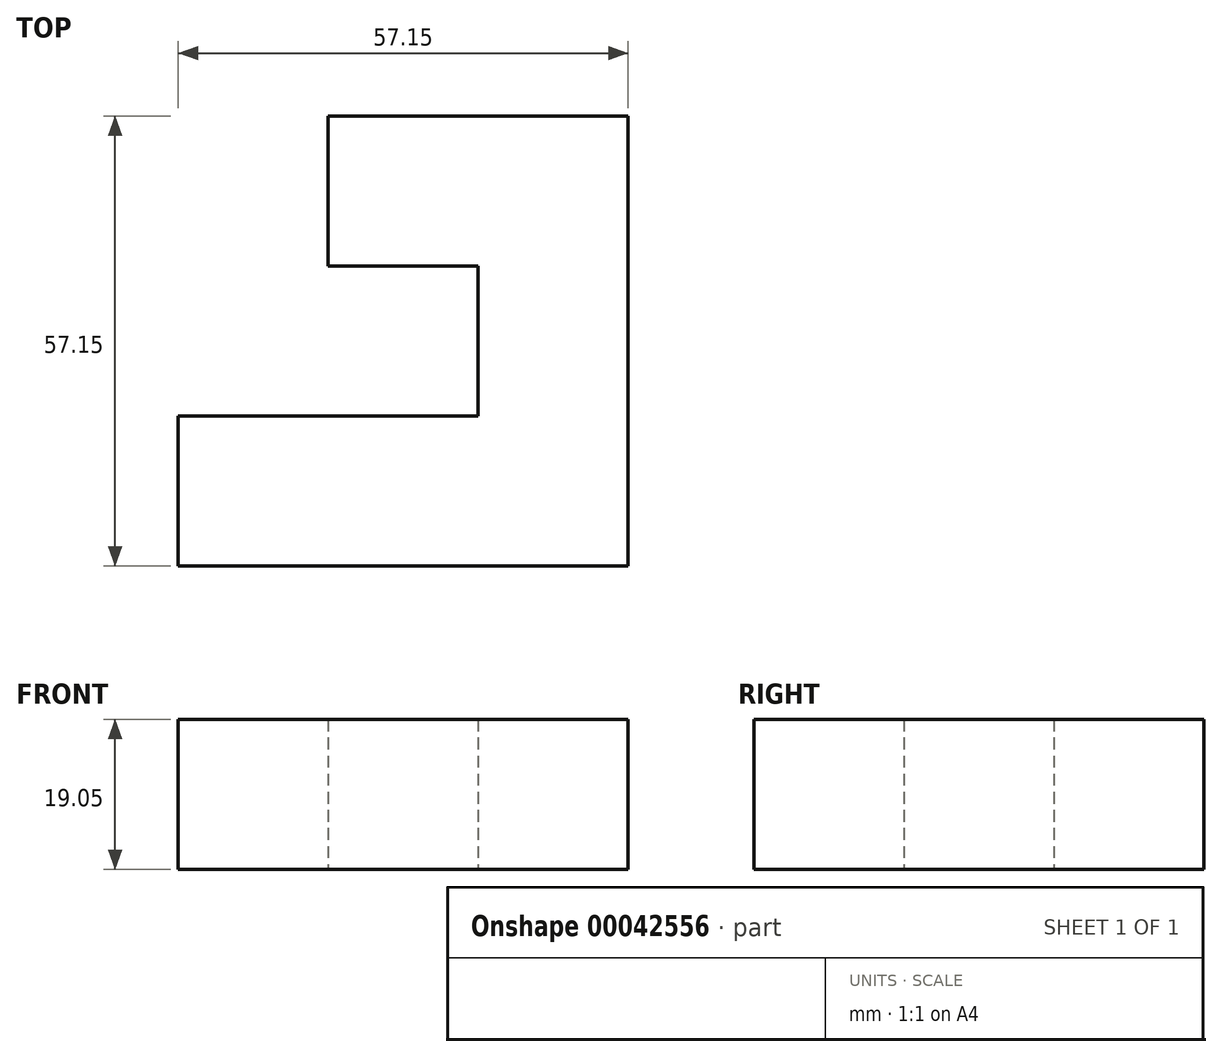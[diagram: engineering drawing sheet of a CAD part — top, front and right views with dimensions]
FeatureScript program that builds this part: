
annotation { "Feature Type Name" : "Feature", "Feature Type Description" : "" }
export const myFeature = defineFeature(function(context is Context, id is Id, definition is map)
    precondition{}
    {
        {
            var Q0;
            Q0=qCreatedBy(makeId("Top.planeOp"),FACE);
            var sketch = newSketch(context, id + "F0", { "sketchPlane" : qUnion([Q0])});
            skLineSegment(sketch, "E0.bottom", {"start": v(0, 0) * mm, "end": v(57.15, 0) * mm});
            skLineSegment(sketch, "E0.top", {"start": v(0, -19.05) * mm, "end": v(57.15, -19.05) * mm});
            skLineSegment(sketch, "E0.left", {"start": v(0, 0) * mm, "end": v(0, -19.05) * mm});
            skLineSegment(sketch, "E0.right", {"start": v(57.15, 0) * mm, "end": v(57.15, -19.05) * mm});
            skLineSegment(sketch, "E1.bottom", {"start": v(57.15, 0) * mm, "end": v(38.1, 0) * mm});
            skLineSegment(sketch, "E1.top", {"start": v(57.15, 38.1) * mm, "end": v(38.1, 38.1) * mm});
            skLineSegment(sketch, "E1.left", {"start": v(57.15, 0) * mm, "end": v(57.15, 38.1) * mm});
            skLineSegment(sketch, "E1.right", {"start": v(38.1, 0) * mm, "end": v(38.1, 38.1) * mm});
            skLineSegment(sketch, "E2.bottom", {"start": v(38.1, 38.1) * mm, "end": v(19.05, 38.1) * mm});
            skLineSegment(sketch, "E2.top", {"start": v(38.1, 19.05) * mm, "end": v(19.05, 19.05) * mm});
            skLineSegment(sketch, "E2.left", {"start": v(38.1, 38.1) * mm, "end": v(38.1, 19.05) * mm});
            skLineSegment(sketch, "E2.right", {"start": v(19.05, 38.1) * mm, "end": v(19.05, 19.05) * mm});
            skSolve(sketch);
        }
        {
            var Q0;
            Q0=qSketchRegion(id+"F0",true);
            extrude(context, id + "F1", {"entities" : qUnion([Q0]), "depth" : 19.05 * mm});
        }
    });
